# Revit family: Electrical-Box_FSR_WM-UTR1S
name_source: partatom
category: Electrical Fixtures
units: mm (PartAtom-declared; Revit-internal decimal feet)

## family parameters
Always vertical = No
Classification Number = 23.85.10.17.11
Cut with Voids When Loaded = No
Maintain Annotation Orientation = No
Part Type = Normal
Room Calculation Point = No
Round Connector Dimension = Use Diameter
Shared = No
Work Plane-Based = Yes

## types (1)
- as Specified
    Assembly Code = D5020100
    Body Material = Metal - Aluminum - Painted Black
    Construction Details = https://www.arcat.com
    Cover Material = Metal - Aluminum - Painted White
    Default Elevation = 0"
    Description = FSR Under Table Rack Shelf - WM-UTR1S as Specified
    Expected Lifespan (Years) = 0
    Green Building-LEED = https://www.arcat.com
    Keynote = 26 27 26
    Maintenance Schedule (Months) = 0
    Manufacturer = FSR Inc.
    Manufacturer Fax = 973-785-4207
    Manufacturer Website = http://www.fsrinc.com
    Model = WM-UTR1S
    Product Data = http://www.arcat.com
    Sales Information = https://fsrinc.com
    Specification = https://www.arcat.com
    Type Comments = 1 RU Mounting Area
    URL = http://www.fsrinc.com
    Unit Depth = 17 11/16"
    Unit Height = 2 5/16"
    Unit Width = 23"
    Warranty Duration (Years) = 0

## geometry (parser evidence)
native form markers: Sweep x3
no freeform markers — native parametric forms only
